# Revit family: 35. Plumbing_Fixtures_Grohe_Concealed_Valve_29032000_14_METRIC
name_source: partatom
category: Pipe Accessories
revit_build: Autodesk Revit 2014 (Build: 20130308_1515(x64)
units: mm (PartAtom-declared; Revit-internal decimal feet)

## types (1)
- Concealed Stop Valve 3/4"
    Assembly Code = D20
    AssetType = Fixed
    Cap Depth = 60 mm
    Cap Dia = 45 mm  [stored 0.147638 ft]
    Cap Material = UHMW, Black
    ClassificationName = Uniclass 2015
    ClassificationValue = Pr_65_54_40_13
    Connection Length = 28 mm
    Connection Size = 15 mm  [stored 0.0492126 ft]
    Connector Radius = 8 mm  [stored 0.0262467 ft]
    Description = Concealed Stop Valve 3/4
    DocumentationLiterature = https://specifi.bimstore.co.uk
    DocumentationTechnical = https://specifi.bimstore.co.uk
    DurationUnit = Years
    ExpectedLife = 0
    Fitting Radius = 10 mm  [stored 0.0328084 ft]
    Height = 86 mm
    Inner Radius = 2 mm  [stored 0.00656168 ft]
    Keynote = S90/620
    Left Connector = 25 mm  [stored 0.082021 ft]
    Loss Method = K Coefficient
    Material = DR-Brass
    Model = Concealed Stop Valve 3/4- 29800000
    ModelNumber = 29032000
    NBSDescription = Check Valves
    NBSObjectName = Check Valves
    NBSReference = 90-154-/323
    ProductionYear = 2015
    Right Connector = 25 mm  [stored 0.082021 ft]
    Stem Dia = 34 mm
    Type Comments = Concealed Stop Valve 3/4"
    TypeName = Concealed Stop Valve 3/4- 29800000
    URL = http://www.grohe.co.uk
    Valve Material = Red Brass Rg5
    WarrantyDurationUnit = Years
    Width = 97 mm
    _BIMspec_GUID = 0
    _current revision = 1
    _distributed by = www.bimstore.co.uk

note: [stored X ft] marks values corroborated as IEEE doubles in the binary element streams (Revit-internal decimal feet)

## geometry (parser evidence)
native form markers: Blend x6, Sweep x2
no freeform markers — native parametric forms only
